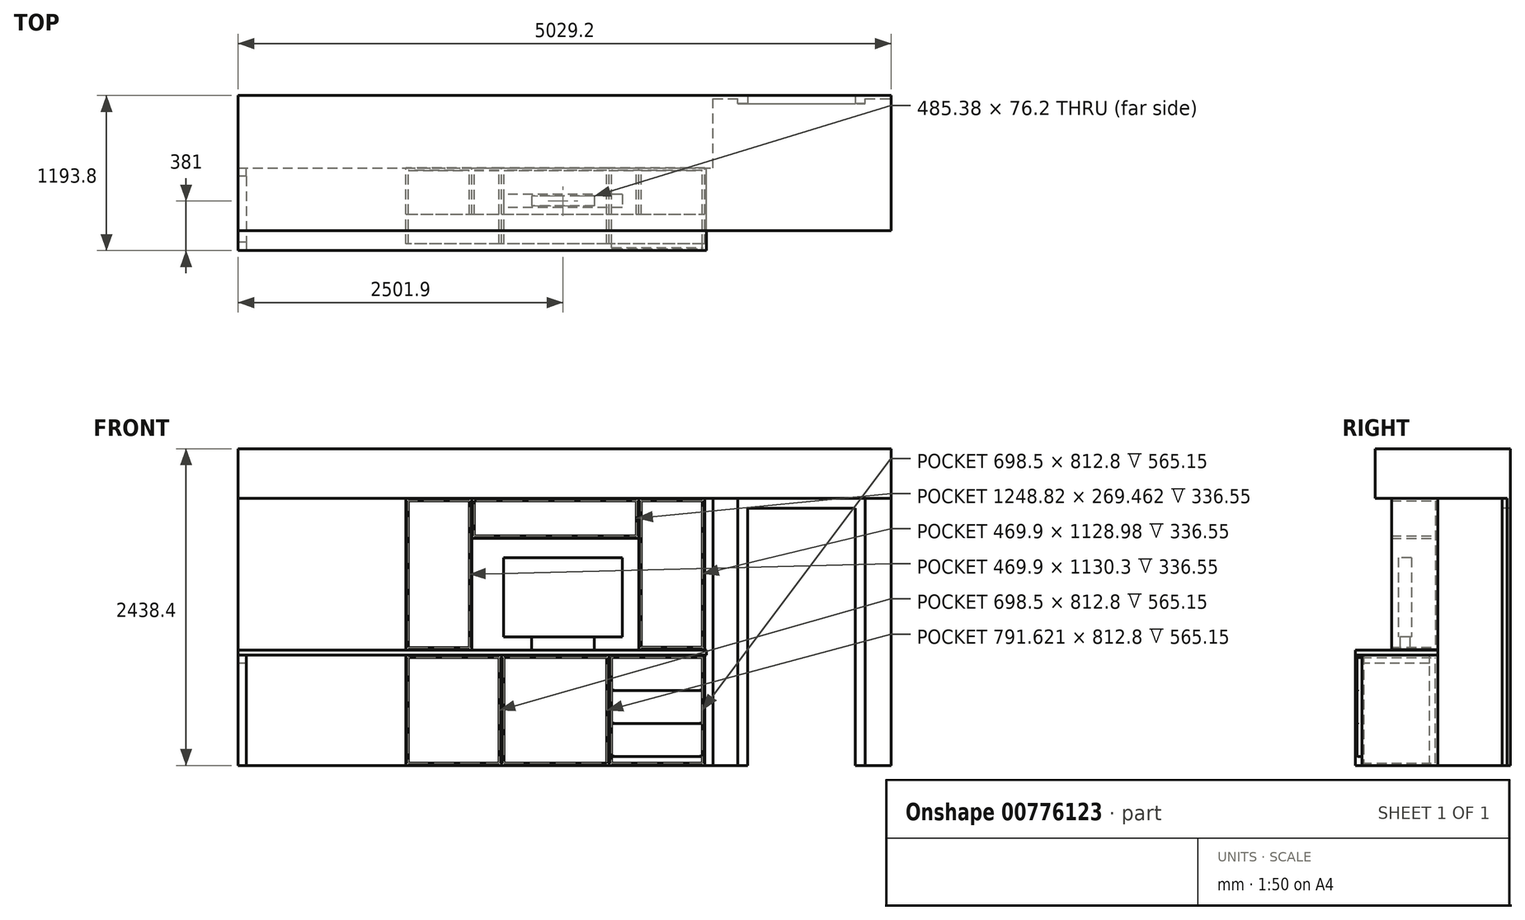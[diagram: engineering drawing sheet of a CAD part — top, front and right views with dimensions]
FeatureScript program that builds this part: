
annotation { "Feature Type Name" : "Feature", "Feature Type Description" : "" }
export const myFeature = defineFeature(function(context is Context, id is Id, definition is map)
    precondition{}
    {
        {
            var Q0;
            Q0=qCreatedBy(makeId("Front.planeOp"),FACE);
            var sketch = newSketch(context, id + "F0", { "sketchPlane" : qUnion([Q0])});
            skLineSegment(sketch, "E0.bottom", {"start": v(2514.6, -1219.2) * mm, "end": v(-2514.6, -1219.2) * mm});
            skLineSegment(sketch, "E0.top", {"start": v(2514.6, 1219.2) * mm, "end": v(-2514.6, 1219.2) * mm});
            skLineSegment(sketch, "E0.left", {"start": v(2514.6, -1219.2) * mm, "end": v(2514.6, 1219.2) * mm});
            skLineSegment(sketch, "E0.right", {"start": v(-2514.6, -1219.2) * mm, "end": v(-2514.6, 1219.2) * mm});
            skPoint(sketch, "E0.middle", {"position": v(0, 0) * mm});
            skSolve(sketch);
        }
        {
            var Q0;
            Q0=makeQuery(id+"F0.imprint","IMPRINT",FACE,{"disambiguationData":[TD([[makeQuery(id+"F0.imprint","IMPRINT",EDGE,{"derivedFrom":sQuery(id+"F0.wireOp",EDGE,"E0.bottom")}),-1.0]])]});
            extrude(context, id + "F1", {"entities" : qUnion([Q0]), "oppositeDirection" : true, "depth" : 25.4 * mm, "offsetDistance" : 25.4 * mm});
        }
        {
            var Q0;
            Q0=makeQuery(id+"F1.opExtrude","CAP_FACE",FACE,{"disambiguationData":[OSD([sQuery(id+"F0.wireOp",EDGE,"E0.bottom"),sQuery(id+"F0.wireOp",EDGE,"E0.top"),sQuery(id+"F0.wireOp",EDGE,"E0.left"),sQuery(id+"F0.wireOp",EDGE,"E0.right")])],"isStart":true});
            var sketch = newSketch(context, id + "F2", { "sketchPlane" : qUnion([Q0])});
            skLineSegment(sketch, "E1.bottom", {"start": v(-2514.6, -1219.2) * mm, "end": v(1143, -1219.2) * mm});
            skLineSegment(sketch, "E1.top", {"start": v(-2514.6, 838.2) * mm, "end": v(1143, 838.2) * mm});
            skLineSegment(sketch, "E1.left", {"start": v(-2514.6, -1219.2) * mm, "end": v(-2514.6, 838.2) * mm});
            skLineSegment(sketch, "E1.right", {"start": v(1143, -1219.2) * mm, "end": v(1143, 838.2) * mm});
            skSolve(sketch);
        }
        {
            var Q0;
            Q0 = qSketchRegion(id + "F2", true);
            extrude(context, id + "F3", {"entities" : qUnion([Q0]), "operationType" : NewBodyOperationType.ADD, "depth" : 533.4 * mm, "offsetDistance" : 25.4 * mm});
        }
        {
            var Q0;
            Q0=makeQuery(id+"F1.opExtrude","CAP_FACE",FACE,{"disambiguationData":[OSD([sQuery(id+"F0.wireOp",EDGE,"E0.bottom"),sQuery(id+"F0.wireOp",EDGE,"E0.top"),sQuery(id+"F0.wireOp",EDGE,"E0.left"),sQuery(id+"F0.wireOp",EDGE,"E0.right")])],"isStart":true});
            var sketch = newSketch(context, id + "F4", { "sketchPlane" : qUnion([Q0])});
            skLineSegment(sketch, "E2.bottom", {"start": v(-2514.6, 838.2) * mm, "end": v(2514.6, 838.2) * mm});
            skLineSegment(sketch, "E2.top", {"start": v(-2514.6, 1219.2) * mm, "end": v(2514.6, 1219.2) * mm});
            skLineSegment(sketch, "E2.left", {"start": v(-2514.6, 838.2) * mm, "end": v(-2514.6, 1219.2) * mm});
            skLineSegment(sketch, "E2.right", {"start": v(2514.6, 838.2) * mm, "end": v(2514.6, 1219.2) * mm});
            skSolve(sketch);
        }
        {
            var Q0;
            Q0=makeQuery(id+"F4.imprint","IMPRINT",FACE,{"disambiguationData":[TD([[makeQuery(id+"F4.imprint","IMPRINT",EDGE,{"derivedFrom":sQuery(id+"F4.wireOp",EDGE,"E2.top")}),1.0]])]});
            extrude(context, id + "F5", {"entities" : qUnion([Q0]), "operationType" : NewBodyOperationType.ADD, "depth" : 1016 * mm, "offsetDistance" : 25.4 * mm});
        }
        {
            var Q0;
            Q0=makeQuery(id+"F1.opExtrude","CAP_FACE",FACE,{"disambiguationData":[OSD([sQuery(id+"F0.wireOp",EDGE,"E0.bottom"),sQuery(id+"F0.wireOp",EDGE,"E0.top"),sQuery(id+"F0.wireOp",EDGE,"E0.left"),sQuery(id+"F0.wireOp",EDGE,"E0.right")])],"isStart":true});
            var sketch = newSketch(context, id + "F6", { "sketchPlane" : qUnion([Q0])});
            skLineSegment(sketch, "E3.bottom", {"start": v(1408.41, -1219.2) * mm, "end": v(2238.54, -1219.2) * mm});
            skLineSegment(sketch, "E3.top", {"start": v(1408.41, 762) * mm, "end": v(2238.54, 762) * mm});
            skLineSegment(sketch, "E3.left", {"start": v(1408.41, -1219.2) * mm, "end": v(1408.41, 762) * mm});
            skLineSegment(sketch, "E3.right", {"start": v(2238.54, -1219.2) * mm, "end": v(2238.54, 762) * mm});
            skSolve(sketch);
        }
        {
            var Q0;
            Q0=makeQuery(id+"F6.imprint","IMPRINT",FACE,{"disambiguationData":[TD([[makeQuery(id+"F6.imprint","IMPRINT",EDGE,{"derivedFrom":sQuery(id+"F6.wireOp",EDGE,"E3.bottom")}),-1.0]])]});
            extrude(context, id + "F7", {"entities" : qUnion([Q0]), "operationType" : NewBodyOperationType.REMOVE, "oppositeDirection" : true, "depth" : 25.4 * mm, "offsetDistance" : 25.4 * mm});
        }
        {
            var Q0;
            Q0=makeQuery(id+"F1.opExtrude","CAP_FACE",FACE,{"disambiguationData":[OSD([sQuery(id+"F0.wireOp",EDGE,"E0.bottom"),sQuery(id+"F0.wireOp",EDGE,"E0.top"),sQuery(id+"F0.wireOp",EDGE,"E0.left"),sQuery(id+"F0.wireOp",EDGE,"E0.right")])],"isStart":true});
            var sketch = newSketch(context, id + "F8", { "sketchPlane" : qUnion([Q0])});
            skLineSegment(sketch, "E4.bottom", {"start": v(1332.21, 838.2) * mm, "end": v(2314.74, 838.2) * mm});
            skLineSegment(sketch, "E4.top", {"start": v(1332.21, -1219.2) * mm, "end": v(2314.74, -1219.2) * mm});
            skLineSegment(sketch, "E4.left", {"start": v(1332.21, 838.2) * mm, "end": v(1332.21, -1219.2) * mm});
            skLineSegment(sketch, "E4.right", {"start": v(2314.74, 838.2) * mm, "end": v(2314.74, -1219.2) * mm});
            skSolve(sketch);
        }
        {
            var Q0;
            Q0=makeQuery(id+"F8.imprint","IMPRINT",FACE,{"disambiguationData":[TD([[makeQuery(id+"F8.imprint","IMPRINT",EDGE,{"derivedFrom":sQuery(id+"F8.wireOp",EDGE,"E4.bottom")}),-1.0]])]});
            extrude(context, id + "F9", {"entities" : qUnion([Q0]), "operationType" : NewBodyOperationType.ADD, "depth" : 38.1 * mm, "offsetDistance" : 25.4 * mm});
        }
        {
            var Q0;
            Q0=makeQuery(id+"F3.opExtrude","CAP_FACE",FACE,{"disambiguationData":[OSD([sQuery(id+"F2.wireOp",EDGE,"E1.bottom"),sQuery(id+"F2.wireOp",EDGE,"E1.top"),sQuery(id+"F2.wireOp",EDGE,"E1.left"),sQuery(id+"F2.wireOp",EDGE,"E1.right")])],"isStart":false});
            var sketch = newSketch(context, id + "F10", { "sketchPlane" : qUnion([Q0])});
            skLineSegment(sketch, "E5.bottom", {"start": v(-2514.6, -368.3) * mm, "end": v(1092.2, -368.3) * mm});
            skLineSegment(sketch, "E5.top", {"start": v(-2514.6, -330.2) * mm, "end": v(1092.2, -330.2) * mm});
            skLineSegment(sketch, "E5.left", {"start": v(-2514.6, -330.2) * mm, "end": v(-2514.6, -368.3) * mm});
            skLineSegment(sketch, "E5.right", {"start": v(1092.2, -330.2) * mm, "end": v(1092.2, -368.3) * mm});
            skSolve(sketch);
        }
        {
            var Q0;
            Q0=makeQuery(id+"F10.imprint","IMPRINT",FACE,{"disambiguationData":[TD([[makeQuery(id+"F10.imprint","IMPRINT",EDGE,{"derivedFrom":sQuery(id+"F10.wireOp",EDGE,"E5.bottom")}),1.0]])]});
            var Q1;
            Q1=sQuery(id+"F10.wireOp",EDGE,"E5.bottom");
            extrude(context, id + "F11", {"entities" : qUnion([Q0]), "surfaceEntities" : qUnion([Q1]), "depth" : 635 * mm, "offsetDistance" : 25.4 * mm});
        }
        {
            var Q0;
            Q0=makeQuery(id+"F3.opExtrude","CAP_FACE",FACE,{"disambiguationData":[OSD([sQuery(id+"F2.wireOp",EDGE,"E1.bottom"),sQuery(id+"F2.wireOp",EDGE,"E1.top"),sQuery(id+"F2.wireOp",EDGE,"E1.left"),sQuery(id+"F2.wireOp",EDGE,"E1.right")])],"isStart":false});
            var sketch = newSketch(context, id + "F12", { "sketchPlane" : qUnion([Q0])});
            skLineSegment(sketch, "E6.bottom", {"start": v(-2514.6, -368.3) * mm, "end": v(-2451.1, -368.3) * mm});
            skLineSegment(sketch, "E6.top", {"start": v(-2514.6, -1219.2) * mm, "end": v(-2451.1, -1219.2) * mm});
            skLineSegment(sketch, "E6.left", {"start": v(-2514.6, -368.3) * mm, "end": v(-2514.6, -1219.2) * mm});
            skLineSegment(sketch, "E6.right", {"start": v(-2451.1, -368.3) * mm, "end": v(-2451.1, -1219.2) * mm});
            skSolve(sketch);
        }
        {
            var Q0;
            Q0=makeQuery(id+"F12.imprint","IMPRINT",FACE,{"disambiguationData":[TD([[makeQuery(id+"F12.imprint","IMPRINT",EDGE,{"derivedFrom":sQuery(id+"F12.wireOp",EDGE,"E6.bottom")}),-1.0]])]});
            extrude(context, id + "F13", {"entities" : qUnion([Q0]), "depth" : 63.5 * mm, "offsetDistance" : 25.4 * mm});
        }
        {
            var Q0;
            Q0=makeQuery(id+"F13.opExtrude","SWEPT_FACE",FACE,{"disambiguationData":[OSD([sQuery(id+"F12.wireOp",EDGE,"E6.left")])]});
            var sketch = newSketch(context, id + "F14", { "sketchPlane" : qUnion([Q0])});
            skLineSegment(sketch, "E7.bottom", {"start": v(596.9, -368.3) * mm, "end": v(1104.9, -368.3) * mm});
            skLineSegment(sketch, "E7.top", {"start": v(596.9, -431.8) * mm, "end": v(1104.9, -431.8) * mm});
            skLineSegment(sketch, "E7.left", {"start": v(596.9, -368.3) * mm, "end": v(596.9, -431.8) * mm});
            skLineSegment(sketch, "E7.right", {"start": v(1104.9, -368.3) * mm, "end": v(1104.9, -431.8) * mm});
            skSolve(sketch);
        }
        {
            var Q0;
            Q0=makeQuery(id+"F14.imprint","IMPRINT",FACE,{"disambiguationData":[TD([[makeQuery(id+"F14.imprint","IMPRINT",EDGE,{"derivedFrom":sQuery(id+"F14.wireOp",EDGE,"E7.bottom")}),-1.0]])]});
            extrude(context, id + "F15", {"entities" : qUnion([Q0]), "oppositeDirection" : true, "depth" : 63.5 * mm, "offsetDistance" : 25.4 * mm});
        }
        {
            var Q0;
            Q0=makeQuery(id+"F15.opExtrude","CAP_FACE",FACE,{"disambiguationData":[OSD([sQuery(id+"F14.wireOp",EDGE,"E7.bottom"),sQuery(id+"F14.wireOp",EDGE,"E7.top"),sQuery(id+"F14.wireOp",EDGE,"E7.left"),sQuery(id+"F14.wireOp",EDGE,"E7.right")])],"isStart":true});
            var sketch = newSketch(context, id + "F16", { "sketchPlane" : qUnion([Q0])});
            skLineSegment(sketch, "E8.bottom", {"start": v(1104.9, -368.3) * mm, "end": v(1168.4, -368.3) * mm});
            skLineSegment(sketch, "E8.top", {"start": v(1104.9, -1219.2) * mm, "end": v(1168.4, -1219.2) * mm});
            skLineSegment(sketch, "E8.left", {"start": v(1104.9, -368.3) * mm, "end": v(1104.9, -1219.2) * mm});
            skLineSegment(sketch, "E8.right", {"start": v(1168.4, -368.3) * mm, "end": v(1168.4, -1219.2) * mm});
            skSolve(sketch);
        }
        {
            var Q0;
            {var subQ1=sQuery(id+"F16.wireOp",EDGE,"E8.bottom");Q0=makeQuery(id+"F16.imprint","IMPRINT",FACE,{"disambiguationData":[TD([[makeQuery(id+"F16.imprint","IMPRINT",EDGE,{"derivedFrom":subQ1}),-1.0]])]});}
            extrude(context, id + "F17", {"entities" : qUnion([Q0]), "oppositeDirection" : true, "depth" : 63.5 * mm, "offsetDistance" : 25.4 * mm});
        }
        {
            var Q0;
            Q0=makeQuery(id+"F3.opExtrude","CAP_FACE",FACE,{"disambiguationData":[OSD([sQuery(id+"F2.wireOp",EDGE,"E1.bottom"),sQuery(id+"F2.wireOp",EDGE,"E1.top"),sQuery(id+"F2.wireOp",EDGE,"E1.left"),sQuery(id+"F2.wireOp",EDGE,"E1.right")])],"isStart":false});
            var sketch = newSketch(context, id + "F18", { "sketchPlane" : qUnion([Q0])});
            skLineSegment(sketch, "E9.bottom", {"start": v(342.9, -1219.2) * mm, "end": v(1079.5, -1219.2) * mm});
            skLineSegment(sketch, "E9.top", {"start": v(342.9, -368.3) * mm, "end": v(1079.5, -368.3) * mm});
            skLineSegment(sketch, "E9.left", {"start": v(342.9, -1219.2) * mm, "end": v(342.9, -368.3) * mm});
            skLineSegment(sketch, "E9.right", {"start": v(1079.5, -1219.2) * mm, "end": v(1079.5, -368.3) * mm});
            skSolve(sketch);
        }
        {
            var Q0;
            Q0 = qSketchRegion(id + "F18", true);
            extrude(context, id + "F19", {"entities" : qUnion([Q0]), "depth" : 584.2 * mm, "offsetDistance" : 25.4 * mm});
        }
        {
            var Q0;
            Q0=makeQuery(id+"F19.opExtrude","CAP_FACE",FACE,{"disambiguationData":[OSD([sQuery(id+"F18.wireOp",EDGE,"E9.bottom"),sQuery(id+"F18.wireOp",EDGE,"E9.top"),sQuery(id+"F18.wireOp",EDGE,"E9.left"),sQuery(id+"F18.wireOp",EDGE,"E9.right")])],"isStart":false});
            shell(context, id + "F20", {"entities" : qUnion([Q0]), "thickness" : 19.05 * mm});
        }
        {
            var Q0;
            Q0=makeQuery(id+"F3.opExtrude","CAP_FACE",FACE,{"disambiguationData":[OSD([sQuery(id+"F2.wireOp",EDGE,"E1.bottom"),sQuery(id+"F2.wireOp",EDGE,"E1.top"),sQuery(id+"F2.wireOp",EDGE,"E1.left"),sQuery(id+"F2.wireOp",EDGE,"E1.right")])],"isStart":false});
            var sketch = newSketch(context, id + "F21", { "sketchPlane" : qUnion([Q0])});
            skLineSegment(sketch, "E10.bottom", {"start": v(342.9, -1219.2) * mm, "end": v(-486.82, -1219.2) * mm});
            skLineSegment(sketch, "E10.top", {"start": v(342.9, -368.3) * mm, "end": v(-486.82, -368.3) * mm});
            skLineSegment(sketch, "E10.left", {"start": v(342.9, -1219.2) * mm, "end": v(342.9, -368.3) * mm});
            skLineSegment(sketch, "E10.right", {"start": v(-486.82, -1219.2) * mm, "end": v(-486.82, -368.3) * mm});
            skSolve(sketch);
        }
        {
            var Q0;
            Q0 = qSketchRegion(id + "F21", true);
            extrude(context, id + "F22", {"entities" : qUnion([Q0]), "depth" : 584.2 * mm, "offsetDistance" : 25.4 * mm});
        }
        {
            var Q0;
            Q0=makeQuery(id+"F22.opExtrude","CAP_FACE",FACE,{"disambiguationData":[OSD([sQuery(id+"F21.wireOp",EDGE,"E10.bottom"),sQuery(id+"F21.wireOp",EDGE,"E10.top"),sQuery(id+"F21.wireOp",EDGE,"E10.left"),sQuery(id+"F21.wireOp",EDGE,"E10.right")])],"isStart":false});
            shell(context, id + "F23", {"entities" : qUnion([Q0]), "thickness" : 19.05 * mm});
        }
        {
            var Q0;
            Q0=makeQuery(id+"F3.opExtrude","CAP_FACE",FACE,{"disambiguationData":[OSD([sQuery(id+"F2.wireOp",EDGE,"E1.bottom"),sQuery(id+"F2.wireOp",EDGE,"E1.top"),sQuery(id+"F2.wireOp",EDGE,"E1.left"),sQuery(id+"F2.wireOp",EDGE,"E1.right")])],"isStart":false});
            var sketch = newSketch(context, id + "F24", { "sketchPlane" : qUnion([Q0])});
            skLineSegment(sketch, "E11.bottom", {"start": v(-1223.42, -1219.2) * mm, "end": v(-486.82, -1219.2) * mm});
            skLineSegment(sketch, "E11.top", {"start": v(-1223.42, -368.3) * mm, "end": v(-486.82, -368.3) * mm});
            skLineSegment(sketch, "E11.left", {"start": v(-1223.42, -1219.2) * mm, "end": v(-1223.42, -368.3) * mm});
            skLineSegment(sketch, "E11.right", {"start": v(-486.82, -1219.2) * mm, "end": v(-486.82, -368.3) * mm});
            skSolve(sketch);
        }
        {
            var Q0;
            Q0 = qSketchRegion(id + "F24", true);
            extrude(context, id + "F25", {"entities" : qUnion([Q0]), "depth" : 584.2 * mm, "offsetDistance" : 25.4 * mm});
        }
        {
            var Q0;
            Q0=makeQuery(id+"F25.opExtrude","CAP_FACE",FACE,{"disambiguationData":[OSD([sQuery(id+"F24.wireOp",EDGE,"E11.bottom"),sQuery(id+"F24.wireOp",EDGE,"E11.top"),sQuery(id+"F24.wireOp",EDGE,"E11.left"),sQuery(id+"F24.wireOp",EDGE,"E11.right")])],"isStart":false});
            shell(context, id + "F26", {"entities" : qUnion([Q0]), "thickness" : 19.05 * mm});
        }
        {
            var Q0;
            Q0=makeQuery(id+"F19.opExtrude","CAP_FACE",FACE,{"disambiguationData":[OSD([sQuery(id+"F18.wireOp",EDGE,"E9.bottom"),sQuery(id+"F18.wireOp",EDGE,"E9.top"),sQuery(id+"F18.wireOp",EDGE,"E9.left"),sQuery(id+"F18.wireOp",EDGE,"E9.right")])],"isStart":false});
            var sketch = newSketch(context, id + "F27", { "sketchPlane" : qUnion([Q0])});
            skLineSegment(sketch, "E12.bottom", {"start": v(361.95, -387.35) * mm, "end": v(1060.45, -387.35) * mm});
            skLineSegment(sketch, "E12.top", {"start": v(361.95, -641.35) * mm, "end": v(1060.45, -641.35) * mm});
            skLineSegment(sketch, "E12.left", {"start": v(361.95, -387.35) * mm, "end": v(361.95, -641.35) * mm});
            skLineSegment(sketch, "E12.right", {"start": v(1060.45, -387.35) * mm, "end": v(1060.45, -641.35) * mm});
            skSolve(sketch);
        }
        {
            var Q0;
            Q0 = qSketchRegion(id + "F27", true);
            extrude(context, id + "F28", {"entities" : qUnion([Q0]), "depth" : 38.1 * mm, "offsetDistance" : 25.4 * mm});
        }
        {
            var Q0;
            Q0=makeQuery(id+"F11.opExtrude","SWEPT_FACE",FACE,{"disambiguationData":[OSD([sQuery(id+"F10.wireOp",EDGE,"E5.top")])]});
            var sketch = newSketch(context, id + "F29", { "sketchPlane" : qUnion([Q0])});
            skLineSegment(sketch, "E13.bottom", {"start": v(229.99, -749.3) * mm, "end": v(-255.39, -749.3) * mm});
            skLineSegment(sketch, "E13.top", {"start": v(229.99, -825.5) * mm, "end": v(-255.39, -825.5) * mm});
            skLineSegment(sketch, "E13.left", {"start": v(229.99, -749.3) * mm, "end": v(229.99, -825.5) * mm});
            skLineSegment(sketch, "E13.right", {"start": v(-255.39, -749.3) * mm, "end": v(-255.39, -825.5) * mm});
            skPoint(sketch, "E13.middle", {"position": v(-12.7, -787.4) * mm});
            skSolve(sketch);
        }
        {
            var Q0;
            Q0 = qSketchRegion(id + "F29", true);
            extrude(context, id + "F30", {"entities" : qUnion([Q0]), "operationType" : NewBodyOperationType.ADD, "depth" : 101.6 * mm, "offsetDistance" : 25.4 * mm});
        }
        {
            var Q0;
            Q0=makeQuery(id+"F30.opExtrude","CAP_FACE",FACE,{"disambiguationData":[OSD([sQuery(id+"F29.wireOp",EDGE,"E13.bottom"),sQuery(id+"F29.wireOp",EDGE,"E13.top"),sQuery(id+"F29.wireOp",EDGE,"E13.left"),sQuery(id+"F29.wireOp",EDGE,"E13.right")])],"isStart":false});
            var sketch = newSketch(context, id + "F31", { "sketchPlane" : qUnion([Q0])});
            skLineSegment(sketch, "E14.bottom", {"start": v(444.5, -735.63) * mm, "end": v(-469.9, -735.63) * mm});
            skLineSegment(sketch, "E14.top", {"start": v(444.5, -837.23) * mm, "end": v(-469.9, -837.23) * mm});
            skLineSegment(sketch, "E14.left", {"start": v(444.5, -735.63) * mm, "end": v(444.5, -837.23) * mm});
            skLineSegment(sketch, "E14.right", {"start": v(-469.9, -735.63) * mm, "end": v(-469.9, -837.23) * mm});
            skPoint(sketch, "E14.middle", {"position": v(-12.7, -786.43) * mm});
            skPoint(sketch, "E14.middle.positionSnap0", {"position": v(-12.7, -749.3) * mm});
            skPoint(sketch, "E14.centerSnap0", {"position": v(-12.7, -749.3) * mm});
            skSolve(sketch);
        }
        {
            var Q0;
            Q0 = qSketchRegion(id + "F31", true);
            extrude(context, id + "F32", {"entities" : qUnion([Q0]), "operationType" : NewBodyOperationType.ADD, "depth" : 609.6 * mm, "offsetDistance" : 25.4 * mm});
        }
        {
            var Q0;
            Q0=makeQuery(id+"F3.opExtrude","CAP_FACE",FACE,{"disambiguationData":[OSD([sQuery(id+"F2.wireOp",EDGE,"E1.bottom"),sQuery(id+"F2.wireOp",EDGE,"E1.top"),sQuery(id+"F2.wireOp",EDGE,"E1.left"),sQuery(id+"F2.wireOp",EDGE,"E1.right")])],"isStart":false});
            var sketch = newSketch(context, id + "F33", { "sketchPlane" : qUnion([Q0])});
            skLineSegment(sketch, "E15.bottom", {"start": v(571.5, 838.2) * mm, "end": v(1079.5, 838.2) * mm});
            skLineSegment(sketch, "E15.top", {"start": v(571.5, -328.88) * mm, "end": v(1079.5, -328.88) * mm});
            skLineSegment(sketch, "E15.left", {"start": v(571.5, 838.2) * mm, "end": v(571.5, -328.88) * mm});
            skLineSegment(sketch, "E15.right", {"start": v(1079.5, 838.2) * mm, "end": v(1079.5, -328.88) * mm});
            skSolve(sketch);
        }
        {
            var Q0;
            Q0=makeQuery(id+"F33.imprint","IMPRINT",FACE,{"disambiguationData":[TD([[makeQuery(id+"F33.imprint","IMPRINT",EDGE,{"derivedFrom":sQuery(id+"F33.wireOp",EDGE,"E15.bottom")}),-1.0]])]});
            extrude(context, id + "F34", {"entities" : qUnion([Q0]), "depth" : 355.6 * mm, "offsetDistance" : 25.4 * mm});
        }
        {
            var Q0;
            Q0=makeQuery(id+"F34.opExtrude","CAP_FACE",FACE,{"disambiguationData":[OSD([sQuery(id+"F33.wireOp",EDGE,"E15.bottom"),sQuery(id+"F33.wireOp",EDGE,"E15.top"),sQuery(id+"F33.wireOp",EDGE,"E15.left"),sQuery(id+"F33.wireOp",EDGE,"E15.right")])],"isStart":false});
            shell(context, id + "F35", {"entities" : qUnion([Q0]), "thickness" : 19.05 * mm});
        }
        {
            var Q0;
            Q0=makeQuery(id+"F3.opExtrude","CAP_FACE",FACE,{"disambiguationData":[OSD([sQuery(id+"F2.wireOp",EDGE,"E1.bottom"),sQuery(id+"F2.wireOp",EDGE,"E1.top"),sQuery(id+"F2.wireOp",EDGE,"E1.left"),sQuery(id+"F2.wireOp",EDGE,"E1.right")])],"isStart":false});
            var sketch = newSketch(context, id + "F36", { "sketchPlane" : qUnion([Q0])});
            skLineSegment(sketch, "E16.bottom", {"start": v(-1223.42, 838.2) * mm, "end": v(-715.42, 838.2) * mm});
            skLineSegment(sketch, "E16.top", {"start": v(-1223.42, -330.2) * mm, "end": v(-715.42, -330.2) * mm});
            skLineSegment(sketch, "E16.left", {"start": v(-1223.42, 838.2) * mm, "end": v(-1223.42, -330.2) * mm});
            skLineSegment(sketch, "E16.right", {"start": v(-715.42, 838.2) * mm, "end": v(-715.42, -330.2) * mm});
            skSolve(sketch);
        }
        {
            var Q0;
            Q0 = qSketchRegion(id + "F36", true);
            extrude(context, id + "F37", {"entities" : qUnion([Q0]), "depth" : 355.6 * mm, "offsetDistance" : 25.4 * mm});
        }
        {
            var Q0;
            Q0=makeQuery(id+"F37.opExtrude","CAP_FACE",FACE,{"disambiguationData":[OSD([sQuery(id+"F36.wireOp",EDGE,"E16.bottom"),sQuery(id+"F36.wireOp",EDGE,"E16.top"),sQuery(id+"F36.wireOp",EDGE,"E16.left"),sQuery(id+"F36.wireOp",EDGE,"E16.right")])],"isStart":false});
            shell(context, id + "F38", {"entities" : qUnion([Q0]), "thickness" : 19.05 * mm});
        }
        {
            var Q0;
            Q0=makeQuery(id+"F3.opExtrude","CAP_FACE",FACE,{"disambiguationData":[OSD([sQuery(id+"F2.wireOp",EDGE,"E1.bottom"),sQuery(id+"F2.wireOp",EDGE,"E1.top"),sQuery(id+"F2.wireOp",EDGE,"E1.left"),sQuery(id+"F2.wireOp",EDGE,"E1.right")])],"isStart":false});
            var sketch = newSketch(context, id + "F39", { "sketchPlane" : qUnion([Q0])});
            skLineSegment(sketch, "E17.bottom", {"start": v(571.5, 838.2) * mm, "end": v(-715.42, 838.2) * mm});
            skLineSegment(sketch, "E17.top", {"start": v(571.5, 530.64) * mm, "end": v(-715.42, 530.64) * mm});
            skLineSegment(sketch, "E17.left", {"start": v(571.5, 838.2) * mm, "end": v(571.5, 530.64) * mm});
            skLineSegment(sketch, "E17.right", {"start": v(-715.42, 838.2) * mm, "end": v(-715.42, 530.64) * mm});
            skSolve(sketch);
        }
        {
            var Q0;
            Q0 = qSketchRegion(id + "F39", true);
            extrude(context, id + "F40", {"entities" : qUnion([Q0]), "depth" : 355.6 * mm, "offsetDistance" : 25.4 * mm});
        }
        {
            var Q0;
            Q0=makeQuery(id+"F40.opExtrude","CAP_FACE",FACE,{"disambiguationData":[OSD([sQuery(id+"F39.wireOp",EDGE,"E17.bottom"),sQuery(id+"F39.wireOp",EDGE,"E17.top"),sQuery(id+"F39.wireOp",EDGE,"E17.left"),sQuery(id+"F39.wireOp",EDGE,"E17.right")])],"isStart":false});
            shell(context, id + "F41", {"entities" : qUnion([Q0]), "thickness" : 19.05 * mm});
        }
        {
            var Q0;
            Q0=makeQuery(id+"F28.opExtrude","CAP_FACE",FACE,{"disambiguationData":[OSD([sQuery(id+"F27.wireOp",EDGE,"E12.bottom"),sQuery(id+"F27.wireOp",EDGE,"E12.top"),sQuery(id+"F27.wireOp",EDGE,"E12.left"),sQuery(id+"F27.wireOp",EDGE,"E12.right")])],"isStart":false});
            fillet(context, id + "F42", {"entities" : qUnion([Q0]), "radius" : 10.16 * mm, "tangentPropagation" : true, "allowEdgeOverflow" : false});
        }
        {
            var Q0;
            Q0=makeQuery(id+"F19.opExtrude","CAP_FACE",FACE,{"disambiguationData":[OSD([sQuery(id+"F18.wireOp",EDGE,"E9.bottom"),sQuery(id+"F18.wireOp",EDGE,"E9.top"),sQuery(id+"F18.wireOp",EDGE,"E9.left"),sQuery(id+"F18.wireOp",EDGE,"E9.right")])],"isStart":false});
            var sketch = newSketch(context, id + "F43", { "sketchPlane" : qUnion([Q0])});
            skLineSegment(sketch, "E18.bottom", {"start": v(361.95, -641.35) * mm, "end": v(1060.45, -641.35) * mm});
            skLineSegment(sketch, "E18.top", {"start": v(361.95, -895.35) * mm, "end": v(1060.45, -895.35) * mm});
            skLineSegment(sketch, "E18.left", {"start": v(361.95, -641.35) * mm, "end": v(361.95, -895.35) * mm});
            skLineSegment(sketch, "E18.right", {"start": v(1060.45, -641.35) * mm, "end": v(1060.45, -895.35) * mm});
            skSolve(sketch);
        }
        {
            var Q0;
            Q0 = qSketchRegion(id + "F43", true);
            extrude(context, id + "F44", {"entities" : qUnion([Q0]), "operationType" : NewBodyOperationType.ADD, "depth" : 38.1 * mm, "offsetDistance" : 25.4 * mm});
        }
        {
            var Q0;
            Q0=makeQuery(id+"F44.opExtrude","CAP_EDGE",EDGE,{"disambiguationData":[OSD([sQuery(id+"F43.wireOp",EDGE,"E18.right")])],"isStart":false});
            var Q1;
            Q1=makeQuery(id+"F44.opExtrude","CAP_FACE",FACE,{"disambiguationData":[OSD([sQuery(id+"F43.wireOp",EDGE,"E18.bottom"),sQuery(id+"F43.wireOp",EDGE,"E18.top"),sQuery(id+"F43.wireOp",EDGE,"E18.left"),sQuery(id+"F43.wireOp",EDGE,"E18.right")])],"isStart":false});
            fillet(context, id + "F45", {"entities" : qUnion([Q0, Q1]), "radius" : 10.16 * mm, "tangentPropagation" : true, "allowEdgeOverflow" : false});
        }
        {
            var Q0;
            Q0=makeQuery(id+"F19.opExtrude","CAP_FACE",FACE,{"disambiguationData":[OSD([sQuery(id+"F18.wireOp",EDGE,"E9.bottom"),sQuery(id+"F18.wireOp",EDGE,"E9.top"),sQuery(id+"F18.wireOp",EDGE,"E9.left"),sQuery(id+"F18.wireOp",EDGE,"E9.right")])],"isStart":false});
            var sketch = newSketch(context, id + "F46", { "sketchPlane" : qUnion([Q0])});
            skLineSegment(sketch, "E19.bottom", {"start": v(361.95, -895.35) * mm, "end": v(1060.45, -895.35) * mm});
            skLineSegment(sketch, "E19.top", {"start": v(361.95, -1149.35) * mm, "end": v(1060.45, -1149.35) * mm});
            skLineSegment(sketch, "E19.left", {"start": v(361.95, -895.35) * mm, "end": v(361.95, -1149.35) * mm});
            skLineSegment(sketch, "E19.right", {"start": v(1060.45, -895.35) * mm, "end": v(1060.45, -1149.35) * mm});
            skSolve(sketch);
        }
        {
            var Q0;
            Q0 = qSketchRegion(id + "F46", true);
            extrude(context, id + "F47", {"entities" : qUnion([Q0]), "operationType" : NewBodyOperationType.ADD, "depth" : 38.1 * mm, "offsetDistance" : 25.4 * mm});
        }
        {
            var Q0;
            Q0=makeQuery(id+"F47.opExtrude","CAP_FACE",FACE,{"disambiguationData":[OSD([sQuery(id+"F46.wireOp",EDGE,"E19.bottom"),sQuery(id+"F46.wireOp",EDGE,"E19.top"),sQuery(id+"F46.wireOp",EDGE,"E19.left"),sQuery(id+"F46.wireOp",EDGE,"E19.right")])],"isStart":false});
            fillet(context, id + "F48", {"entities" : qUnion([Q0]), "radius" : 10.16 * mm, "tangentPropagation" : true, "allowEdgeOverflow" : false});
        }
    });
